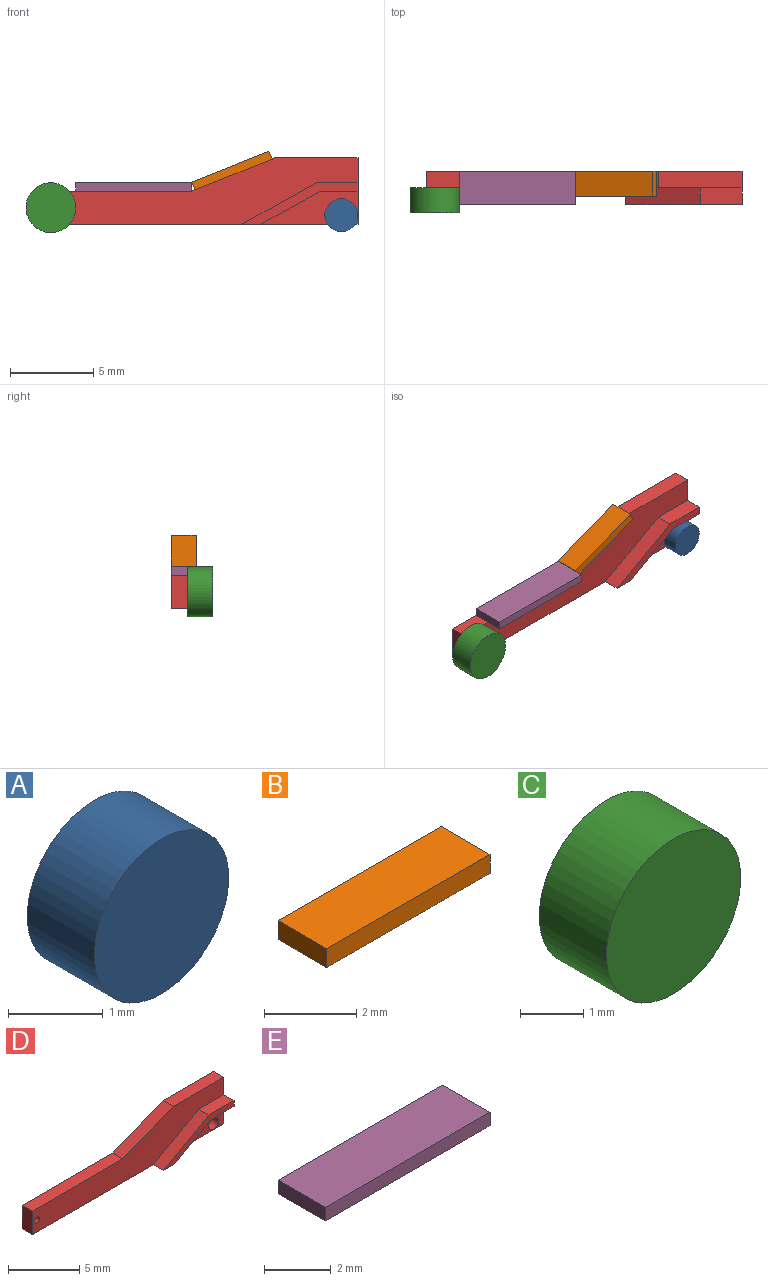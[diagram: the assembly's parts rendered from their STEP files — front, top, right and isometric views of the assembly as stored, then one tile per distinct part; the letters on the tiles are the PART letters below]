
ASSEMBLY  parts=5 mates=4
PART A: 3 faces, bbox 2x1x2 mm
  f0: cylinder r=1mm len=2mm, axis (0,1,0), area 6.3mm2, adj f1,f2
  f1: plane 2x2mm, normal (0,-1,0), area 3.1mm2, adj f0
  f2: plane 2x2mm, normal (0,1,0), area 3.1mm2, adj f0
PART B: 6 faces, bbox 5x1.5x0.5 mm
  f0: plane 1.5x0.5mm, normal (1,0,0), area 0.8mm2, adj f1,f3,f4,f5
  f1: plane 5x0.5mm, normal (0,1,0), area 2.5mm2, adj f0,f2,f4,f5
  f2: plane 1.5x0.5mm, normal (-1,0,0), area 0.8mm2, adj f1,f3,f4,f5
  f3: plane 5x0.5mm, normal (0,-1,0), area 2.5mm2, adj f0,f2,f4,f5
  f4: plane 5x1.5mm, normal (0,0,1), area 7.5mm2, adj f0,f1,f2,f3
  f5: plane 5x1.5mm, normal (0,0,-1), area 7.5mm2, adj f0,f1,f2,f3
PART C: 3 faces, bbox 3x1.5x3 mm
  f0: cylinder r=1.5mm len=3mm, axis (0,1,0), area 14.1mm2, adj f1,f2
  f1: plane 3x3mm, normal (0,-1,0), area 7.1mm2, adj f0
  f2: plane 3x3mm, normal (0,1,0), area 7.1mm2, adj f0
PART D: 16 faces, bbox 19x2x4 mm
  f0: plane 19x4mm, normal (0,-1,0), area 40.9mm2, adj f2,f3,f4,f5,f6,f7,f8,f13
  f1: plane 5.85x2mm, normal (0,-1,0), area 7.3mm2, adj f2,f3,f9,f11,f12
  f2: plane 19x2mm, normal (0,0,-1), area 20.1mm2, adj f0,f1,f3,f8,f10,f11,f14,f15
  f3: plane 4x2mm, normal (1,0,0), area 4.5mm2, adj f0,f1,f2,f4,f10,f12,f13,f15
  f4: plane 5x1mm, normal (0,0,1), area 5mm2, adj f0,f3,f5,f10
  f5: plane 5x2mm, normal (-0.37,0,0.93), area 5.4mm2, adj f0,f4,f6,f10
  f6: plane 9x1mm, normal (0,0,1), area 9mm2, adj f0,f5,f8,f10
  f7: cylinder r=0.25mm len=1mm, axis (0,1,0), area 1.6mm2, adj f0,f10
  f8: plane 2x1mm, normal (-1,0,0), area 2mm2, adj f0,f2,f6,f10
  f9: cylinder r=0.5mm len=1mm, axis (0,1,0), area 3.1mm2, adj f1,f10
  f10: plane 19x4mm, normal (0,1,0), area 52mm2, adj f2,f3,f4,f5,f6,f7,f8,f9
  f11: plane 3.6x2mm, normal (0.49,0,-0.87), area 4.1mm2, adj f1,f2,f12,f15
  f12: plane 2.25x1mm, normal (0,0,-1), area 2.3mm2, adj f1,f3,f11,f15
  f13: plane 2.5x1mm, normal (0,0,1), area 2.5mm2, adj f0,f3,f14,f15
  f14: plane 4.5x2.5mm, normal (-0.49,0,0.87), area 5.1mm2, adj f0,f2,f13,f15
  f15: plane 7x2.5mm, normal (0,-1,0), area 3.8mm2, adj f2,f3,f11,f12,f13,f14
PART E: 6 faces, bbox 7x2x0.5 mm
  f0: plane 2x0.5mm, normal (-1,0,0), area 1mm2, adj f1,f3,f4,f5
  f1: plane 7x0.5mm, normal (0,-1,0), area 3.5mm2, adj f0,f2,f4,f5
  f2: plane 2x0.5mm, normal (1,0,0), area 1mm2, adj f1,f3,f4,f5
  f3: plane 7x0.5mm, normal (0,1,0), area 3.5mm2, adj f0,f2,f4,f5
  f4: plane 7x2mm, normal (0,0,1), area 14mm2, adj f0,f1,f2,f3
  f5: plane 7x2mm, normal (0,0,-1), area 14mm2, adj f0,f1,f2,f3
PLACE A t=(10.13,0.51,1.93)mm
PLACE B rot(axis=(0,-1,0),21.8deg) t=(3.63,0.76,4.38)mm
PLACE C t=(-7.37,0.51,2.38)mm
PLACE D t=(4.13,1.51,1.38)mm
PLACE E t=(-5.87,-0.49,3.38)mm
MATE fastened E.f5 <-> D.f6  axis (0,0,-1) through (-2.37,0.51,3.38)mm
MATE cylindrical C.f0 <-> D.f7  axis (0,1,0) through (-7.37,0.51,2.38)mm
MATE cylindrical A.f0 <-> D.f9  axis (0,1,0) through (10.13,0.51,1.93)mm
MATE fastened B.f5 <-> D.f5  axis (0.37,0,-0.93) through (3.63,0.76,4.38)mm
